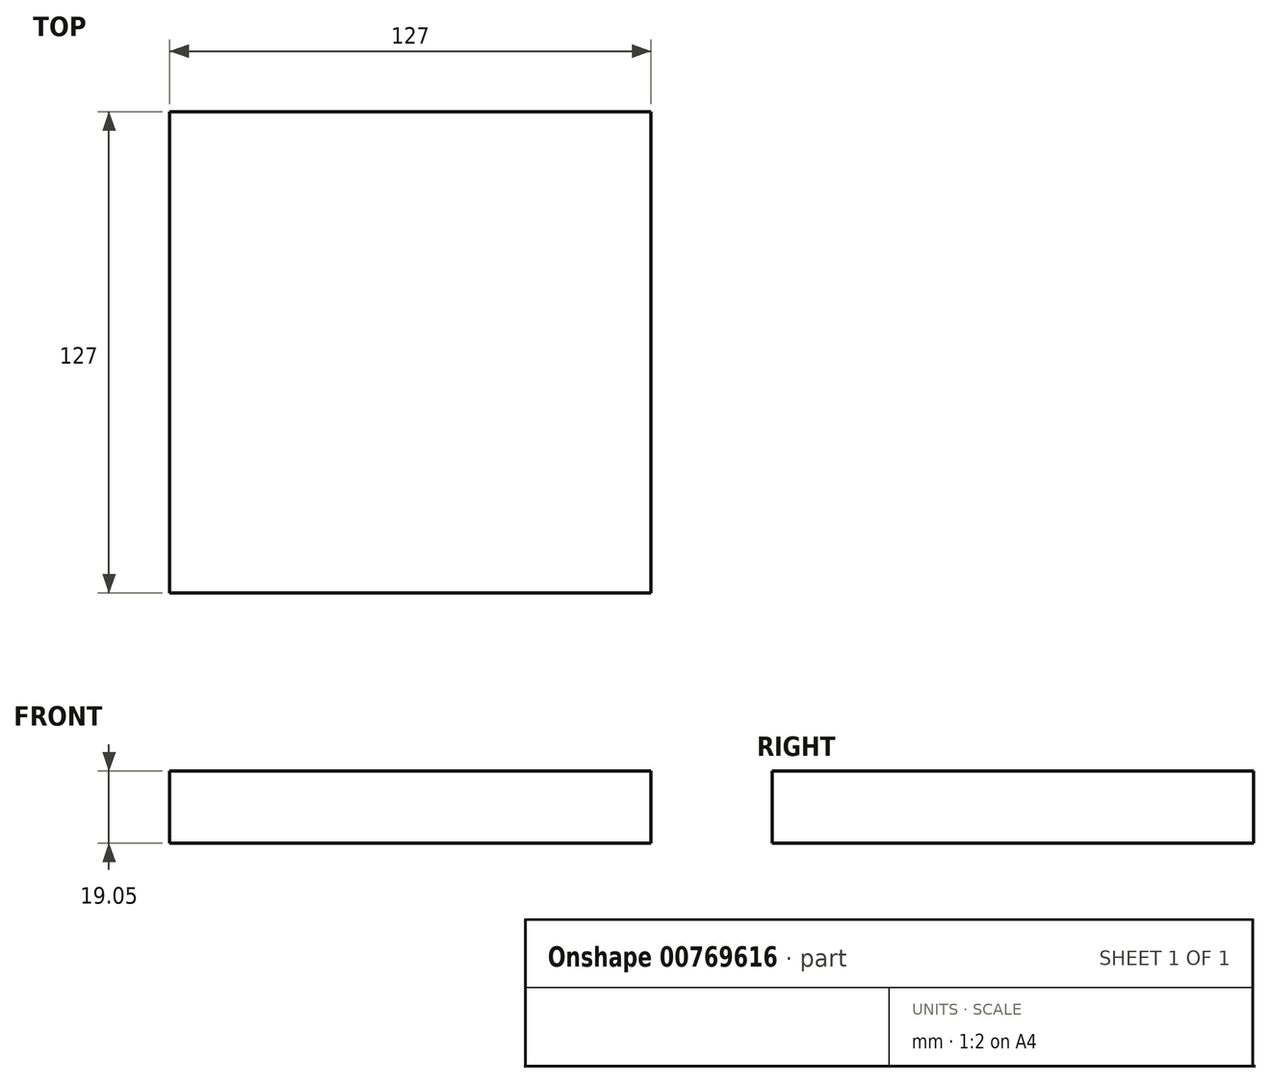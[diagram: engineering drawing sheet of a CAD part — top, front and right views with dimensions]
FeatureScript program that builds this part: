
annotation { "Feature Type Name" : "Feature", "Feature Type Description" : "" }
export const myFeature = defineFeature(function(context is Context, id is Id, definition is map)
    precondition{}
    {
        {
            var Q0;
            Q0=qCreatedBy(makeId("Top.planeOp"),FACE);
            var sketch = newSketch(context, id + "F0", { "sketchPlane" : qUnion([Q0])});
            skLineSegment(sketch, "E0.bottom", {"start": v(-66.22, -47.02) * mm, "end": v(60.78, -47.02) * mm});
            skLineSegment(sketch, "E0.top", {"start": v(-66.22, 79.98) * mm, "end": v(60.78, 79.98) * mm});
            skLineSegment(sketch, "E0.left", {"start": v(-66.22, -47.02) * mm, "end": v(-66.22, 79.98) * mm});
            skLineSegment(sketch, "E0.right", {"start": v(60.78, -47.02) * mm, "end": v(60.78, 79.98) * mm});
            skSolve(sketch);
        }
        {
            var Q0;
            Q0=makeQuery(id+"F0.imprint","IMPRINT",FACE,{"disambiguationData":[TD([[makeQuery(id+"F0.imprint","IMPRINT",EDGE,{"derivedFrom":sQuery(id+"F0.wireOp",EDGE,"E0.bottom")}),1.0]])]});
            extrude(context, id + "F1", {"entities" : qUnion([Q0]), "depth" : 19.05 * mm, "offsetDistance" : 25.4 * mm});
        }
    });
